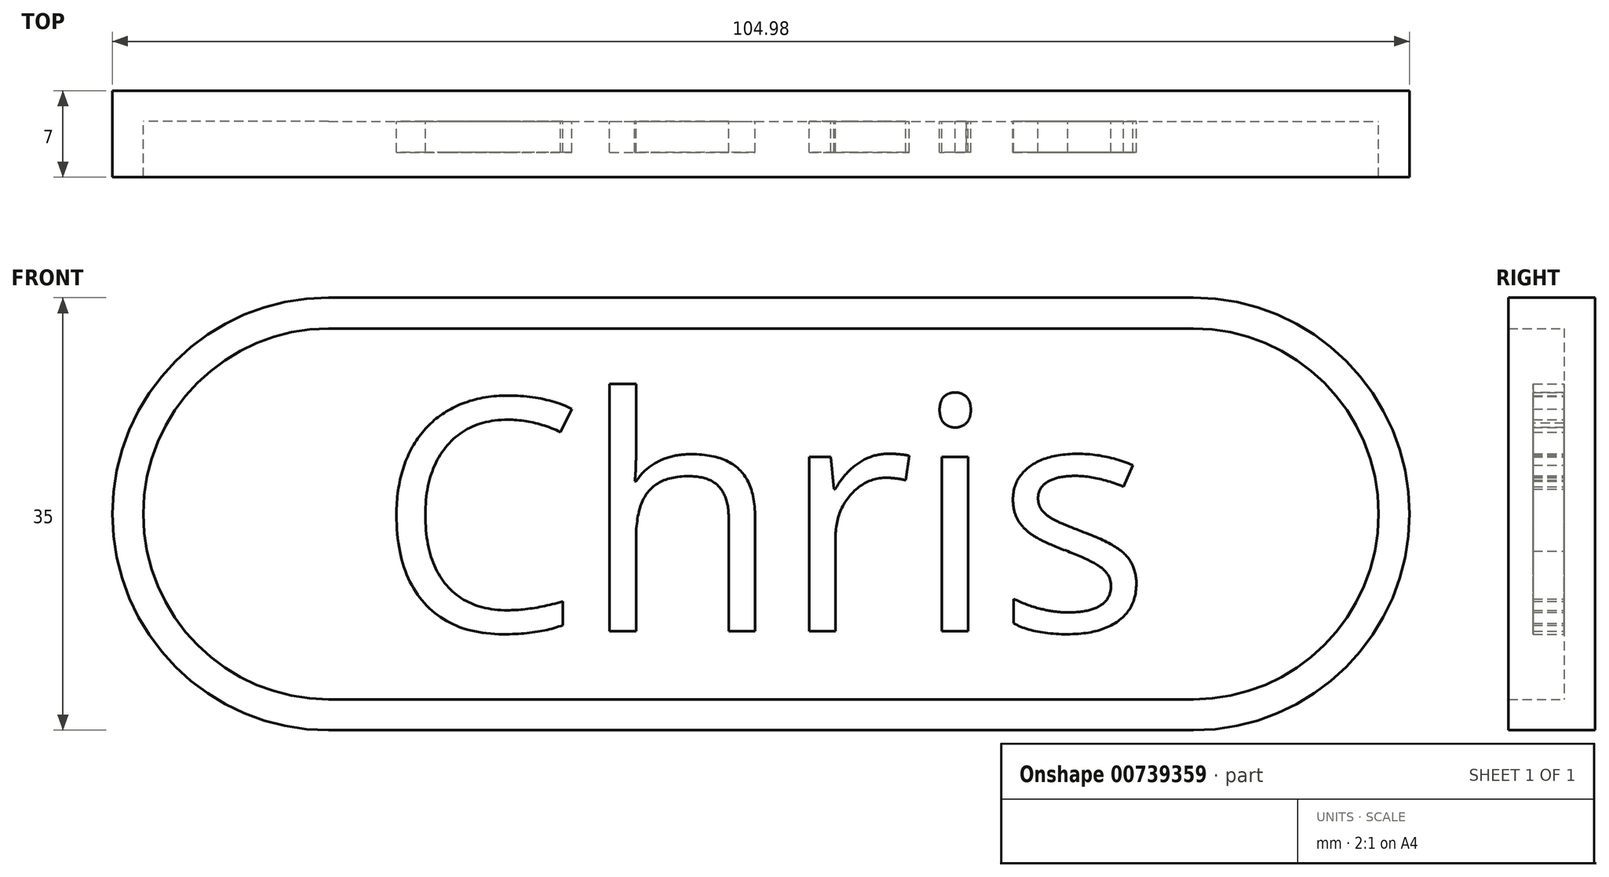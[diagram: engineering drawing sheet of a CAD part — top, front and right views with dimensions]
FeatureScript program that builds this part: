
annotation { "Feature Type Name" : "Feature", "Feature Type Description" : "" }
export const myFeature = defineFeature(function(context is Context, id is Id, definition is map)
    precondition{}
    {
        {
            var Q0;
            Q0=qCreatedBy(makeId("Front.planeOp"),FACE);
            var sketch = newSketch(context, id + "F0", { "sketchPlane" : qUnion([Q0])});
            skArc(sketch, "E0", {"start": v(-34.99, 17.5) * mm, "mid": v(-52.49, 0) * mm, "end": v(-34.99, -17.5) * mm});
            skArc(sketch, "E1.1.0", {"start": v(34.99, -17.5) * mm, "mid": v(52.49, 0) * mm, "end": v(34.99, 17.5) * mm});
            skPoint(sketch, "E1.center", {"position": v(0, 0) * mm});
            skLineSegment(sketch, "E2", {"start": v(-34.99, 17.5) * mm, "end": v(34.99, 17.5) * mm});
            skLineSegment(sketch, "E3", {"start": v(-34.99, -17.5) * mm, "end": v(34.99, -17.5) * mm});
            skSolve(sketch);
        }
        {
            var Q0;
            Q0=makeQuery(id+"F0.imprint","IMPRINT",FACE,{"disambiguationData":[TD([[makeQuery(id+"F0.imprint","IMPRINT",EDGE,{"derivedFrom":sQuery(id+"F0.wireOp",EDGE,"E0")}),1.0]])]});
            extrude(context, id + "F1", {"entities" : qUnion([Q0]), "depth" : 7 * mm, "offsetDistance" : 25 * mm});
        }
        {
            var Q0;
            Q0=makeQuery(id+"F1.opExtrude","CAP_FACE",FACE,{"disambiguationData":[OSD([sQuery(id+"F0.wireOp",EDGE,"E0"),sQuery(id+"F0.wireOp",EDGE,"E1.1.0"),sQuery(id+"F0.wireOp",EDGE,"E2"),sQuery(id+"F0.wireOp",EDGE,"E3")])],"isStart":false});
            shell(context, id + "F2", {"entities" : qUnion([Q0]), "thickness" : 2.5 * mm});
        }
        {
            var Q0;
            Q0=qCreatedBy(makeId("Front.planeOp"),FACE);
            var sketch = newSketch(context, id + "F3", { "sketchPlane" : qUnion([Q0])});
            skText(sketch, "E4", { "text": "Chris", "fontName": "OpenSans-Regular.ttf"});
            const initialGuessF3  = {"E4": [-0.0311, -0.00947, 1, 0, 0.01894]};
            skSetInitialGuess(sketch, initialGuessF3);
            skSolve(sketch);
        }
        {
            var Q0;
            Q0 = qSketchRegion(id + "F3", true);
            extrude(context, id + "F4", {"entities" : qUnion([Q0]), "operationType" : NewBodyOperationType.ADD, "depth" : 5 * mm, "offsetDistance" : 25 * mm});
        }
    });
